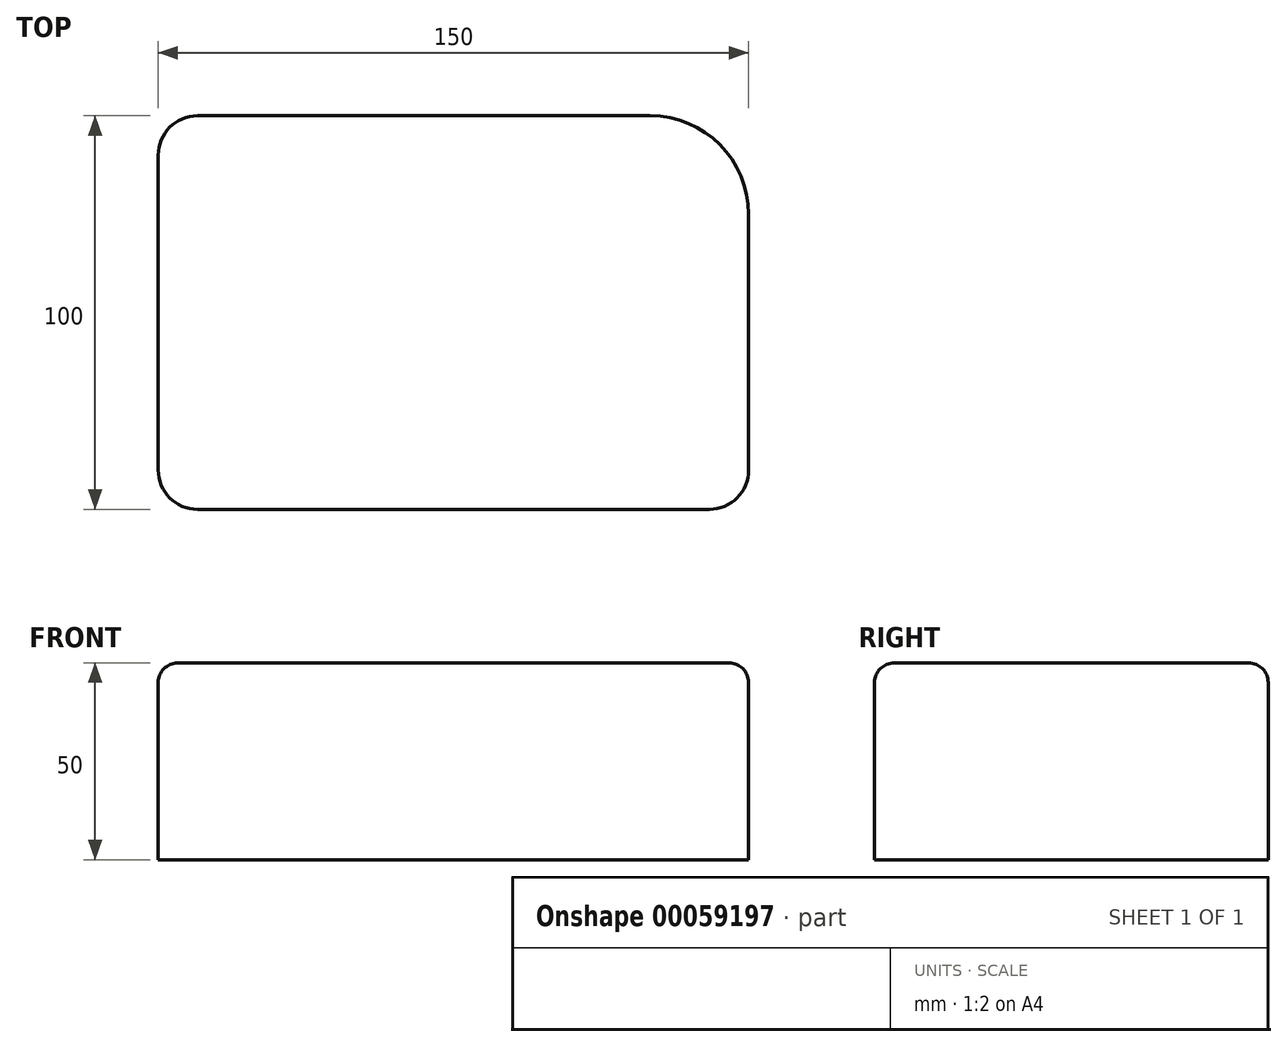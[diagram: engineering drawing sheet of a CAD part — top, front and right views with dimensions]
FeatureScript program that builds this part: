
annotation { "Feature Type Name" : "Feature", "Feature Type Description" : "" }
export const myFeature = defineFeature(function(context is Context, id is Id, definition is map)
    precondition{}
    {
        {
            var Q0;
            Q0=qCreatedBy(makeId("Top.planeOp"),FACE);
            var sketch = newSketch(context, id + "F0", { "sketchPlane" : qUnion([Q0])});
            skLineSegment(sketch, "E0.bottom", {"start": v(-65, -50) * mm, "end": v(65, -50) * mm});
            skLineSegment(sketch, "E0.top", {"start": v(-65, 50) * mm, "end": v(50, 50) * mm});
            skLineSegment(sketch, "E0.left", {"start": v(-75, -40) * mm, "end": v(-75, 40) * mm});
            skLineSegment(sketch, "E0.right", {"start": v(75, -40) * mm, "end": v(75, 25) * mm});
            skPoint(sketch, "E0.middle", {"position": v(0, 0) * mm});
            skPoint(sketch, "E1.visualSharp", {"position": v(-75, 50) * mm});
            skArc(sketch, "E1.filletArc", {"start": v(-65, 50) * mm, "mid": v(-72.07, 47.07) * mm, "end": v(-75, 40) * mm});
            skPoint(sketch, "E2.visualSharp", {"position": v(-75, -50) * mm});
            skArc(sketch, "E2.filletArc", {"start": v(-75, -40) * mm, "mid": v(-72.07, -47.07) * mm, "end": v(-65, -50) * mm});
            skPoint(sketch, "E3.visualSharp", {"position": v(75, -50) * mm});
            skArc(sketch, "E3.filletArc", {"start": v(65, -50) * mm, "mid": v(72.07, -47.07) * mm, "end": v(75, -40) * mm});
            skPoint(sketch, "E4.visualSharp", {"position": v(75, 50) * mm});
            skArc(sketch, "E4.filletArc", {"start": v(75, 25) * mm, "mid": v(67.68, 42.68) * mm, "end": v(50, 50) * mm});
            skSolve(sketch);
        }
        {
            var Q0;
            Q0 = qSketchRegion(id + "F0", true);
            extrude(context, id + "F1", {"entities" : qUnion([Q0]), "depth" : 50 * mm});
        }
        {
            var Q0;
            Q0=makeQuery(id+"F1.opExtrude","CAP_EDGE",EDGE,{"disambiguationData":[OSD([sQuery(id+"F0.wireOp",EDGE,"E0.right")])],"isStart":false});
            fillet(context, id + "F2", {"entities" : qUnion([Q0]), "radius" : 5 * mm, "tangentPropagation" : true, "allowEdgeOverflow" : false});
        }
    });
